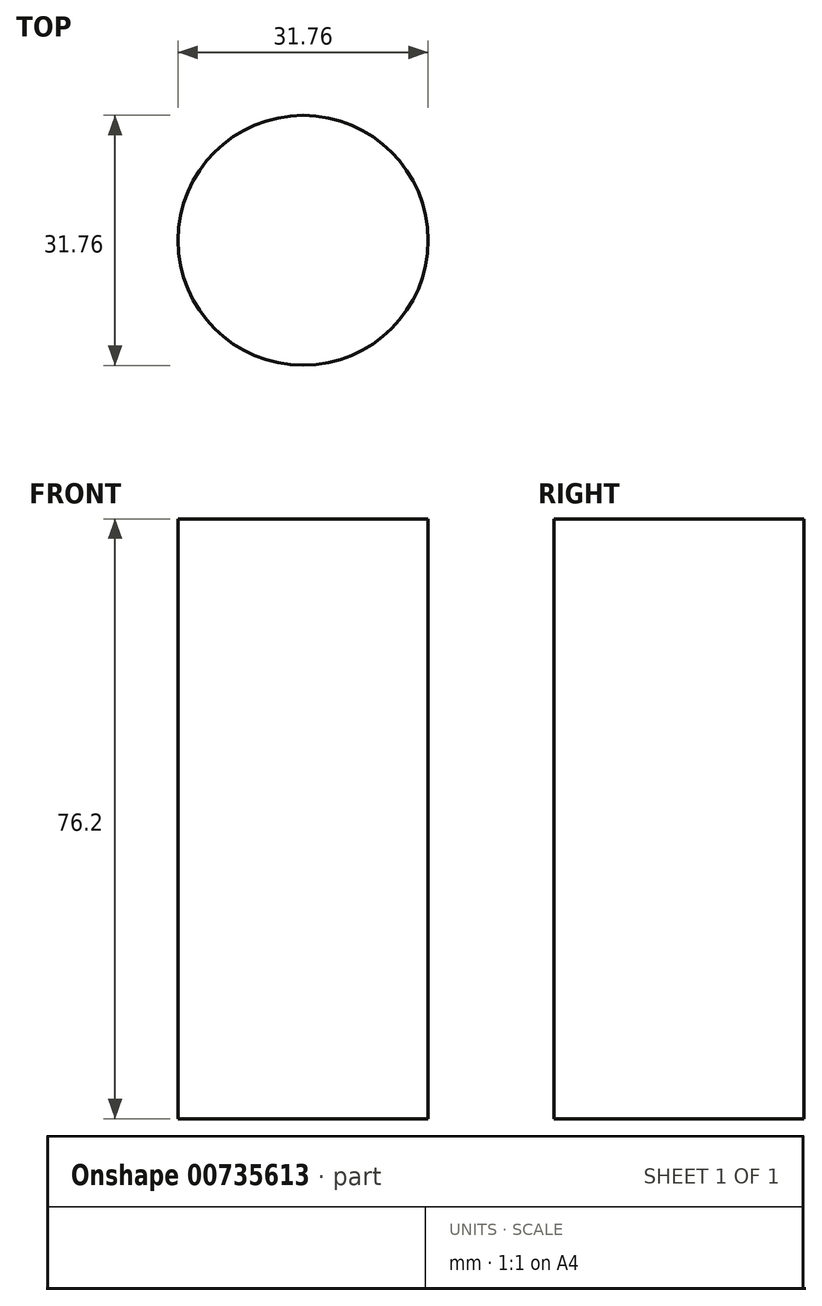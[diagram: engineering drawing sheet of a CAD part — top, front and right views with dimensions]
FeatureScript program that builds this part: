
annotation { "Feature Type Name" : "Feature", "Feature Type Description" : "" }
export const myFeature = defineFeature(function(context is Context, id is Id, definition is map)
    precondition{}
    {
        {
            var Q0;
            Q0=qCreatedBy(makeId("Top.planeOp"),FACE);
            var sketch = newSketch(context, id + "F0", { "sketchPlane" : qUnion([Q0])});
            skCircle(sketch, "E0", {"center": v(0, 0) * mm, "radius": 15.88 * mm});
            skSolve(sketch);
        }
        {
            var Q0;
            Q0 = qSketchRegion(id + "F0", true);
            extrude(context, id + "F1", {"entities" : qUnion([Q0]), "depth" : 76.2 * mm, "offsetDistance" : 25.4 * mm});
        }
    });
